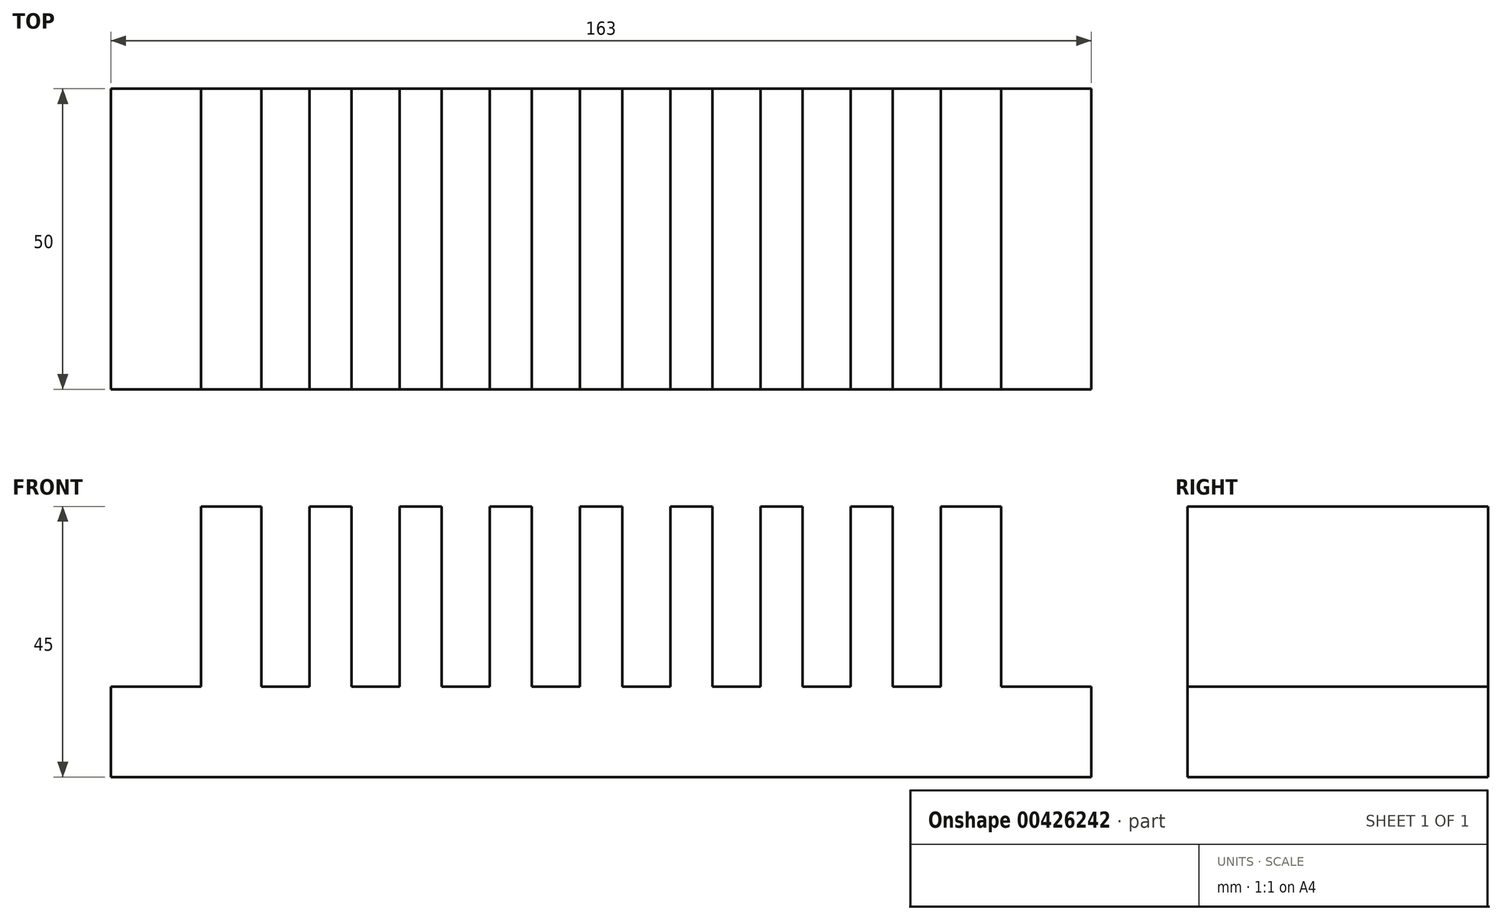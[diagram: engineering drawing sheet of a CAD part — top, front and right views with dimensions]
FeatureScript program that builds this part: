
annotation { "Feature Type Name" : "Feature", "Feature Type Description" : "" }
export const myFeature = defineFeature(function(context is Context, id is Id, definition is map)
    precondition{}
    {
        {
            var Q0;
            Q0=qCreatedBy(makeId("Front.planeOp"),FACE);
            var sketch = newSketch(context, id + "F0", { "sketchPlane" : qUnion([Q0])});
            skLineSegment(sketch, "E0.bottom", {"start": v(81.5, -25) * mm, "end": v(-81.5, -25) * mm});
            skLineSegment(sketch, "E0.top", {"start": v(66.5, 20) * mm, "end": v(56.5, 20) * mm});
            skLineSegment(sketch, "E0.left", {"start": v(81.5, -25) * mm, "end": v(81.5, -10) * mm});
            skLineSegment(sketch, "E0.right", {"start": v(-81.5, -25) * mm, "end": v(-81.5, -10) * mm});
            skLineSegment(sketch, "E1", {"start": v(-81.5, -10) * mm, "end": v(-66.5, -10) * mm});
            skLineSegment(sketch, "E2", {"start": v(-3.5, 20) * mm, "end": v(-3.5, -10) * mm});
            skLineSegment(sketch, "E3.MirrorCS", {"start": v(3.5, 20) * mm, "end": v(3.5, -10) * mm});
            skLineSegment(sketch, "E4", {"start": v(11.5, 20) * mm, "end": v(11.5, -10) * mm});
            skLineSegment(sketch, "E5", {"start": v(18.5, 20) * mm, "end": v(18.5, -10) * mm});
            skLineSegment(sketch, "E6", {"start": v(26.5, 20) * mm, "end": v(26.5, -10) * mm});
            skLineSegment(sketch, "E7", {"start": v(33.5, 20) * mm, "end": v(33.5, -10) * mm});
            skLineSegment(sketch, "E8", {"start": v(41.5, 20) * mm, "end": v(41.5, -10) * mm});
            skLineSegment(sketch, "E9", {"start": v(48.5, 20) * mm, "end": v(48.5, -10) * mm});
            skLineSegment(sketch, "E10", {"start": v(56.5, 20) * mm, "end": v(56.5, -10) * mm});
            skLineSegment(sketch, "E11", {"start": v(66.5, 20) * mm, "end": v(66.5, -10) * mm});
            skLineSegment(sketch, "E12.MirrorCS", {"start": v(-11.5, 20) * mm, "end": v(-11.5, -10) * mm});
            skLineSegment(sketch, "E13.MirrorCS", {"start": v(-18.5, 20) * mm, "end": v(-18.5, -10) * mm});
            skLineSegment(sketch, "E14.MirrorCS", {"start": v(-26.5, 20) * mm, "end": v(-26.5, -10) * mm});
            skLineSegment(sketch, "E15.MirrorCS", {"start": v(-33.5, 20) * mm, "end": v(-33.5, -10) * mm});
            skLineSegment(sketch, "E16.MirrorCS", {"start": v(-41.5, 20) * mm, "end": v(-41.5, -10) * mm});
            skLineSegment(sketch, "E17.MirrorCS", {"start": v(-48.5, 20) * mm, "end": v(-48.5, -10) * mm});
            skLineSegment(sketch, "E18.MirrorCS", {"start": v(-56.5, 20) * mm, "end": v(-56.5, -10) * mm});
            skLineSegment(sketch, "E19.MirrorCS", {"start": v(-66.5, 20) * mm, "end": v(-66.5, -10) * mm});
            skLineSegment(sketch, "E20.trimOffspring", {"start": v(48.5, 20) * mm, "end": v(41.5, 20) * mm});
            skLineSegment(sketch, "E21.trimOffspring", {"start": v(33.5, 20) * mm, "end": v(26.5, 20) * mm});
            skLineSegment(sketch, "E22.trimOffspring", {"start": v(18.5, 20) * mm, "end": v(11.5, 20) * mm});
            skLineSegment(sketch, "E23.trimOffspring", {"start": v(3.5, 20) * mm, "end": v(-3.5, 20) * mm});
            skLineSegment(sketch, "E24.trimOffspring", {"start": v(-11.5, 20) * mm, "end": v(-18.5, 20) * mm});
            skLineSegment(sketch, "E25.trimOffspring", {"start": v(-26.5, 20) * mm, "end": v(-33.5, 20) * mm});
            skLineSegment(sketch, "E26.trimOffspring", {"start": v(-41.5, 20) * mm, "end": v(-48.5, 20) * mm});
            skLineSegment(sketch, "E27.trimOffspring", {"start": v(-56.5, 20) * mm, "end": v(-66.5, 20) * mm});
            skLineSegment(sketch, "E28.trimOffspring", {"start": v(-56.5, -10) * mm, "end": v(-48.5, -10) * mm});
            skLineSegment(sketch, "E29.trimOffspring", {"start": v(-41.5, -10) * mm, "end": v(-33.5, -10) * mm});
            skLineSegment(sketch, "E30.trimOffspring", {"start": v(-26.5, -10) * mm, "end": v(-18.5, -10) * mm});
            skLineSegment(sketch, "E31.trimOffspring", {"start": v(-11.5, -10) * mm, "end": v(-3.5, -10) * mm});
            skLineSegment(sketch, "E32.trimOffspring", {"start": v(3.5, -10) * mm, "end": v(11.5, -10) * mm});
            skLineSegment(sketch, "E33.trimOffspring", {"start": v(18.5, -10) * mm, "end": v(26.5, -10) * mm});
            skLineSegment(sketch, "E34.trimOffspring", {"start": v(33.5, -10) * mm, "end": v(41.5, -10) * mm});
            skLineSegment(sketch, "E35.trimOffspring", {"start": v(48.5, -10) * mm, "end": v(56.5, -10) * mm});
            skLineSegment(sketch, "E36.trimOffspring", {"start": v(66.5, -10) * mm, "end": v(81.5, -10) * mm});
            skSolve(sketch);
        }
        {
            var Q0;
            Q0=makeQuery(id+"F0.imprint","IMPRINT",FACE,{"disambiguationData":[TD([[makeQuery(id+"F0.imprint","IMPRINT",EDGE,{"derivedFrom":sQuery(id+"F0.wireOp",EDGE,"E0.bottom")}),-1.0]])]});
            extrude(context, id + "F1", {"entities" : qUnion([Q0]), "depth" : 50 * mm});
        }
    });
